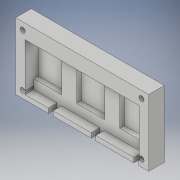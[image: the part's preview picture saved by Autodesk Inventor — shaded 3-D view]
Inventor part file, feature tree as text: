
AUTODESK INVENTOR PART (.ipt)
format: ipt  version: 2018 (Build 220112000, 112)  size: 175,616 bytes
history: native  units: in
note: dims shown in document units (in); Inventor stores cm internally (conversion verified against a paired STEP export)
features: extrude x4, sketch x3, hole x2, pattern_linear x1
ambient origin geometry x8: Origin, YZ Plane, XZ Plane, XY Plane, X Axis, Y Axis, Z Axis, Center Point
bodies: Solid1 (feature_tree)
feature tree (10):
  sketch  "Sketch1"  dims[d0=7.0in d1=3.5in]
  extrude  "Extrusion1"  Depth=3.5in
  extrude  "Extrusion2"  Depth=2.0in
  extrude  "Extrusion3"  Depth=0.5in
  extrude  "Extrusion4"  Depth=0.5in
  pattern_linear  "Rectangular Pattern1"  Spacing1=0.7in  [1 undecoded]
  hole  "Hole2"  [1 undecoded]
  sketch  "Sketch2"  dims[d2=1.475in d3=2.0in]
  sketch  "Sketch3"  dims[d4=0.5in d5=0.5in d6=0.5in d7=0.7in d8=0.0in d9=0.125in d10=0.0in d11=0.25in d12=0.0in d13=0.25in d14=0.25in d15=0.0in d16=1.1811in d18=2.25in d19=0.266in d20=0.75in d21=0.375in d22=0.25in d23=0.5635in d24=1.0in d25=0.0in]
  hole  "Hole1"  [1 undecoded]
note: 3 required parameter values undecoded (feature->parameter linkage not recoverable at this tier; creation-order binding heuristic only, values carry confidence <= 0.55)
